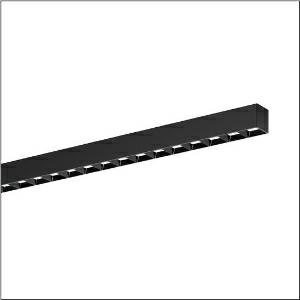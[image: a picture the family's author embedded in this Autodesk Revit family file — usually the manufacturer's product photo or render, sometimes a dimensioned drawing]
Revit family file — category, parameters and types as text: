
# Revit family: silica_21_51mx24tat4b
name_source: partatom
category: Lighting Fixtures
units: mm (PartAtom-declared; Revit-internal decimal feet)

## family parameters
Cut with Voids When Loaded = No
Host = Face
Light Source = No
Part Type = Normal
Room Calculation Point = No
Round Connector Dimension = Use Diameter
Shared = No

## types (1)
- --- (1 x LED, 3280 lm, 32.4 W, 6500K)
    Apparent Load = 32 VA
    CIE Flux Codes = 74 94 99 100 100
    Color Rendering = 80
    Color Temperature = 6500K
    Default Elevation = 1800 mm
    Description = Silica 21, office luminaire, primary light control with darklight reflector, of PMMA, black, light emission: direct distribution, primary light characteristic: asymmetric, installation type: surface-mounted, LED, rated luminous flux: 3.280lm, luminous efficacy: 96lm/W, light colour: 8tw, colour temperature: 2700..6500K, control gear: DALI DT8, with terminal, 3+2-pole, max. 2.5mm², mains connection: 220..240V, AC, 50/60Hz, rated input power: 34.1W, luminaire housing, of aluminium, matt jet black (RAL 9005), length: 1.204mm, width: 53mm, height: 53mm, protection rating (complete): IP20, insulation class (complete): insulation class I (protective earthing), certification: CE, permissible operating ambient temperature: 0..+35°C, standard: EN 50419, packaging unit: 1 piece
    Height = 53 mm
    Lamp = 1 x LED
    Lamp Light Flux = 3280 lm
    Lamp Power = 32.4 W
    Lamp count = 1
    Length = 1204 mm
    Luminous efficacy = 101 lm/W
    Manufacturer = Siteco
    ModVariant = No
    Model = 51MX24TAT4B
    Mounting Place = Ceiling
    Mounting Type = Surface mounted
    Number of Poles = 1
    OnlyDefault = Yes
    Power Factor = 1
    Product Name = Silica 21
    Product group = office luminaire | ceiling mounted
    ProductGroupID = 301
    Protection Class = Protection class I
    Protection Degree = IP 20
    RLX_Detail_Level = 1
    RLX_Emergency_Light_Flux = 0 lm
    RLX_Emergency_Type = 0
    RLX_Emergency_Type_DB = No
    RlxData = <blob elided: 40573 chars, md5=58039f60>
    Socket = socket
    Standby Power = 0 W
    System Light Flux = 3280 lm
    System Power = 32 W
    Type Comments = individual setting
    Type Image = l_1335908.jpg
    URL = http://relux.com
    VarID = @adj_139493
    Voltage = 0 V
    Weight = 0.00 kg
    Width = 53 mm

## geometry (parser evidence)
native form markers: Blend x4, Sweep x9
no freeform markers — native parametric forms only
